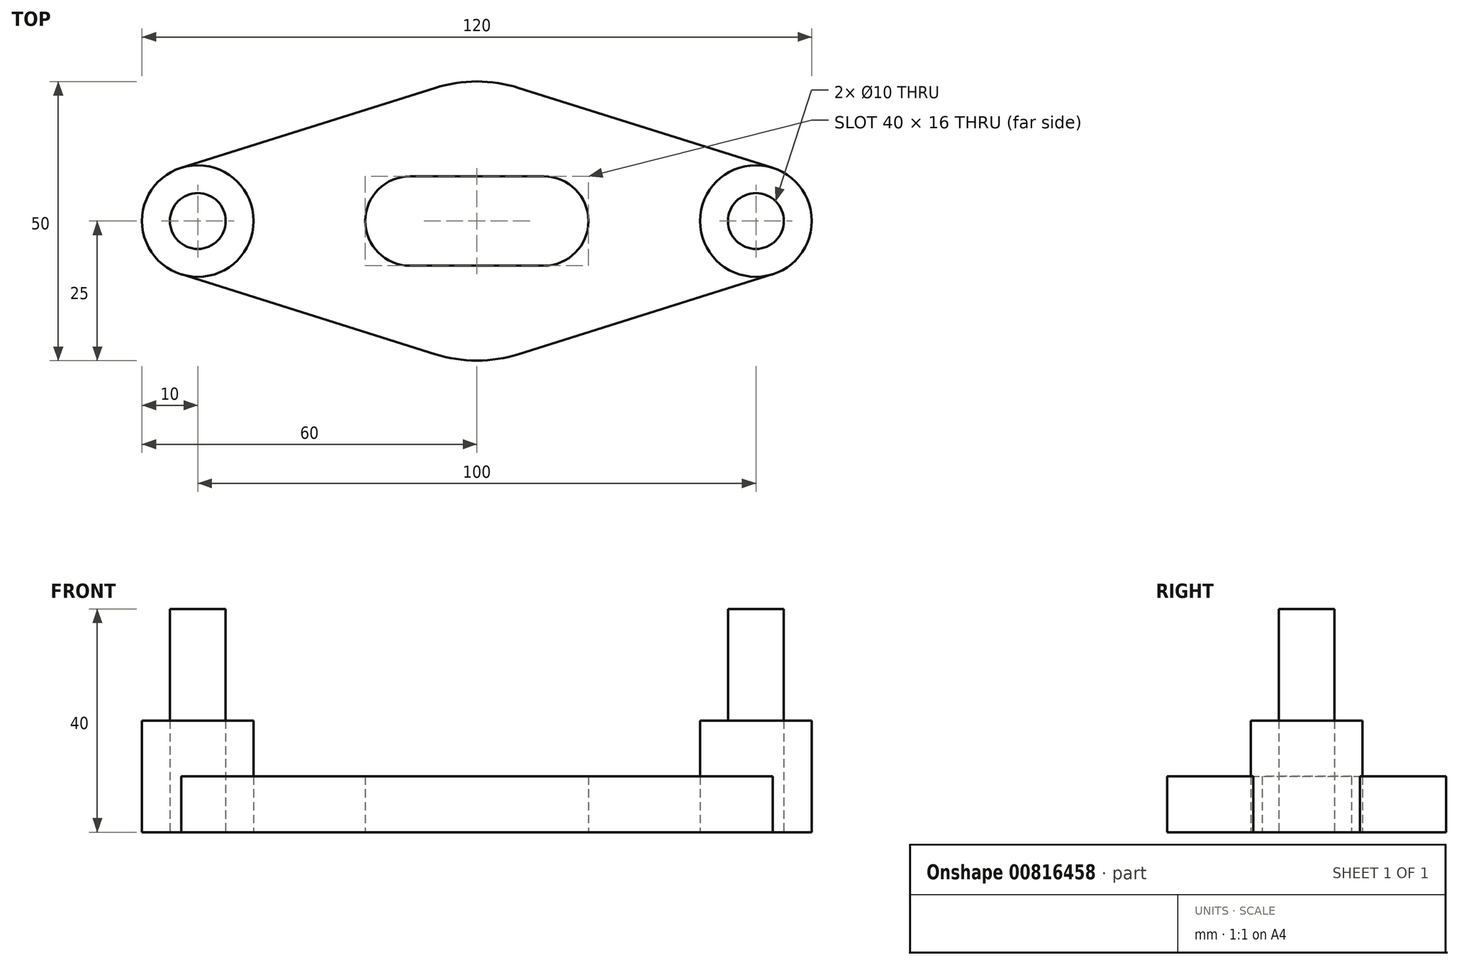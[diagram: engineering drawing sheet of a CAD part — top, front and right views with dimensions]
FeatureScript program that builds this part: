
annotation { "Feature Type Name" : "Feature", "Feature Type Description" : "" }
export const myFeature = defineFeature(function(context is Context, id is Id, definition is map)
    precondition{}
    {
        {
            var Q0;
            Q0=qCreatedBy(makeId("Top.planeOp"),FACE);
            var sketch = newSketch(context, id + "F0", { "sketchPlane" : qUnion([Q0])});
            skArc(sketch, "E0", {"start": v(-7.5, -23.85) * mm, "mid": v(0, -25) * mm, "end": v(7.5, -23.85) * mm});
            skCircle(sketch, "E1", {"center": v(-50, 0) * mm, "radius": 10 * mm});
            skCircle(sketch, "E2", {"center": v(50, 0) * mm, "radius": 10 * mm});
            skArc(sketch, "E3", {"start": v(-12, 8) * mm, "mid": v(-20, 0) * mm, "end": v(-12, -8) * mm});
            skArc(sketch, "E4", {"start": v(12, -8) * mm, "mid": v(20, 0) * mm, "end": v(12, 8) * mm});
            skCircle(sketch, "E5", {"center": v(-50, 0) * mm, "radius": 5 * mm});
            skCircle(sketch, "E6", {"center": v(50, 0) * mm, "radius": 5 * mm});
            skLineSegment(sketch, "E7", {"start": v(-12, 8) * mm, "end": v(12, 8) * mm});
            skLineSegment(sketch, "E8", {"start": v(12, -8) * mm, "end": v(-12, -8) * mm});
            skLineSegment(sketch, "E9", {"start": v(-53, -9.54) * mm, "end": v(-7.5, -23.85) * mm});
            skLineSegment(sketch, "E10", {"start": v(-53, 9.54) * mm, "end": v(-7.5, 23.85) * mm});
            skLineSegment(sketch, "E11", {"start": v(7.07, 23.98) * mm, "end": v(53, 9.54) * mm});
            skLineSegment(sketch, "E12", {"start": v(7.5, -23.85) * mm, "end": v(53, -9.54) * mm});
            skArc(sketch, "E13.trimOffspring", {"start": v(7.5, 23.85) * mm, "mid": v(0, 25) * mm, "end": v(-7.5, 23.85) * mm});
            skPoint(sketch, "E14", {"position": v(-20, 0) * mm});
            skPoint(sketch, "E15", {"position": v(20, 0) * mm});
            skSolve(sketch);
        }
        {
            var Q0;
            Q0=makeQuery(id+"F0.imprint","IMPRINT",FACE,{"disambiguationData":[TD([[makeQuery(id+"F0.imprint","IMPRINT",EDGE,{"derivedFrom":sQuery(id+"F0.wireOp",EDGE,"E5")}),-1.0]])]});
            var Q1;
            Q1=makeQuery(id+"F0.imprint","IMPRINT",FACE,{"disambiguationData":[TD([[makeQuery(id+"F0.imprint","IMPRINT",EDGE,{"derivedFrom":sQuery(id+"F0.wireOp",EDGE,"E6")}),-1.0]])]});
            extrude(context, id + "F1", {"entities" : qUnion([Q0, Q1]), "depth" : 20 * mm, "offsetDistance" : 25 * mm});
        }
        {
            var Q0;
            Q0=makeQuery(id+"F0.imprint","IMPRINT",FACE,{"disambiguationData":[TD([[makeQuery(id+"F0.imprint","IMPRINT",EDGE,{"derivedFrom":sQuery(id+"F0.wireOp",EDGE,"E5")}),1.0]])]});
            var Q1;
            Q1=makeQuery(id+"F0.imprint","IMPRINT",FACE,{"disambiguationData":[TD([[makeQuery(id+"F0.imprint","IMPRINT",EDGE,{"derivedFrom":sQuery(id+"F0.wireOp",EDGE,"E6")}),1.0]])]});
            extrude(context, id + "F2", {"entities" : qUnion([Q0, Q1]), "depth" : 40 * mm, "offsetDistance" : 25 * mm});
        }
        {
            var Q0;
            Q0=makeQuery(id+"F0.imprint","IMPRINT",FACE,{"disambiguationData":[TD([[makeQuery(id+"F0.imprint","IMPRINT",EDGE,{"derivedFrom":sQuery(id+"F0.wireOp",EDGE,"E0")}),1.0]])]});
            extrude(context, id + "F3", {"entities" : qUnion([Q0]), "depth" : 10 * mm, "offsetDistance" : 25 * mm});
        }
    });
